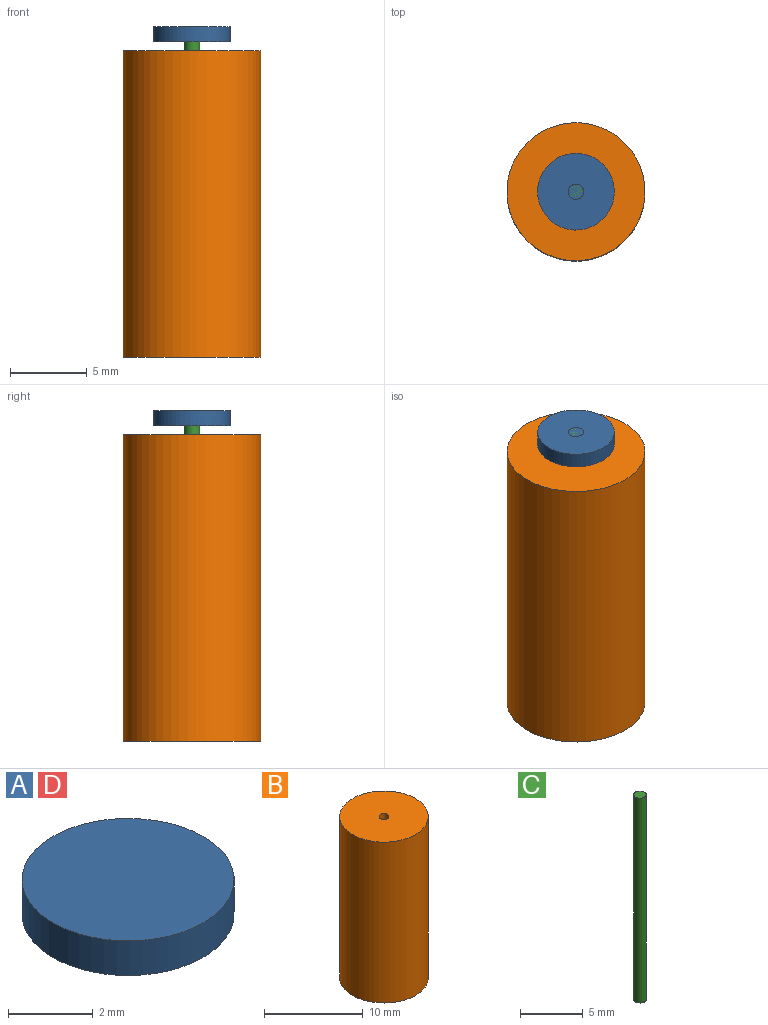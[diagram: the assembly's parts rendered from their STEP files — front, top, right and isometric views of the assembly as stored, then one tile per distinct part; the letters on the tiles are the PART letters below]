
ASSEMBLY  parts=4 mates=3
PART A: 3 faces, bbox 5x5x1 mm
  f0: cylinder r=2.5mm len=5mm, axis (0,0,-1), area 15.7mm2, adj f1,f2
  f1: plane 5x5mm, normal (0,0,1), area 19.6mm2, adj f0
  f2: plane 5x5mm, normal (0,0,-1), area 19.6mm2, adj f0
PART B: 8 faces, bbox 9x9x20 mm
  f0: plane 7x7mm, normal (0,0,1), area 37.7mm2, adj f1,f4
  f1: cylinder r=3.5mm len=18mm, axis (0,0,-1), area 395.8mm2, adj f0,f2
  f2: plane 7x7mm, normal (0,0,-1), area 37.7mm2, adj f1,f3
  f3: cylinder r=0.5mm len=1mm, axis (0,0,1), area 3.1mm2, adj f2,f7
  f4: cylinder r=0.5mm len=1mm, axis (0,0,1), area 3.1mm2, adj f0,f6
  f5: cylinder r=4.5mm len=20mm, axis (0,0,-1), area 565.5mm2, adj f6,f7
  f6: plane 9x9mm, normal (0,0,-1), area 62.8mm2, adj f4,f5
  f7: plane 9x9mm, normal (0,0,1), area 62.8mm2, adj f3,f5
PART C: 3 faces, bbox 1x1x20 mm
  f0: cylinder r=0.5mm len=20mm, axis (0,0,-1), area 62.8mm2, adj f1,f2
  f1: plane 1x1mm, normal (0,0,1), area 0.8mm2, adj f0
  f2: plane 1x1mm, normal (0,0,-1), area 0.8mm2, adj f0
PART D: same geometry as A
PLACE A t=(-1.35,-10.85,18.91)mm
PLACE B t=(-1.35,-10.85,-1.65)mm
PLACE C t=(-1.35,-10.85,-0.09)mm
PLACE D t=(-1.35,-10.85,-1.09)mm
MATE fastened A.f0 <-> C.f0  axis (0,0,1) through (-1.35,-10.85,19.91)mm
MATE fastened D.f0 <-> C.f0  axis (0,0,1) through (-1.35,-10.85,-0.09)mm
MATE slider C.f0 <-> B.f5  axis (0,0,-1) through (-1.35,-10.85,9.91)mm
